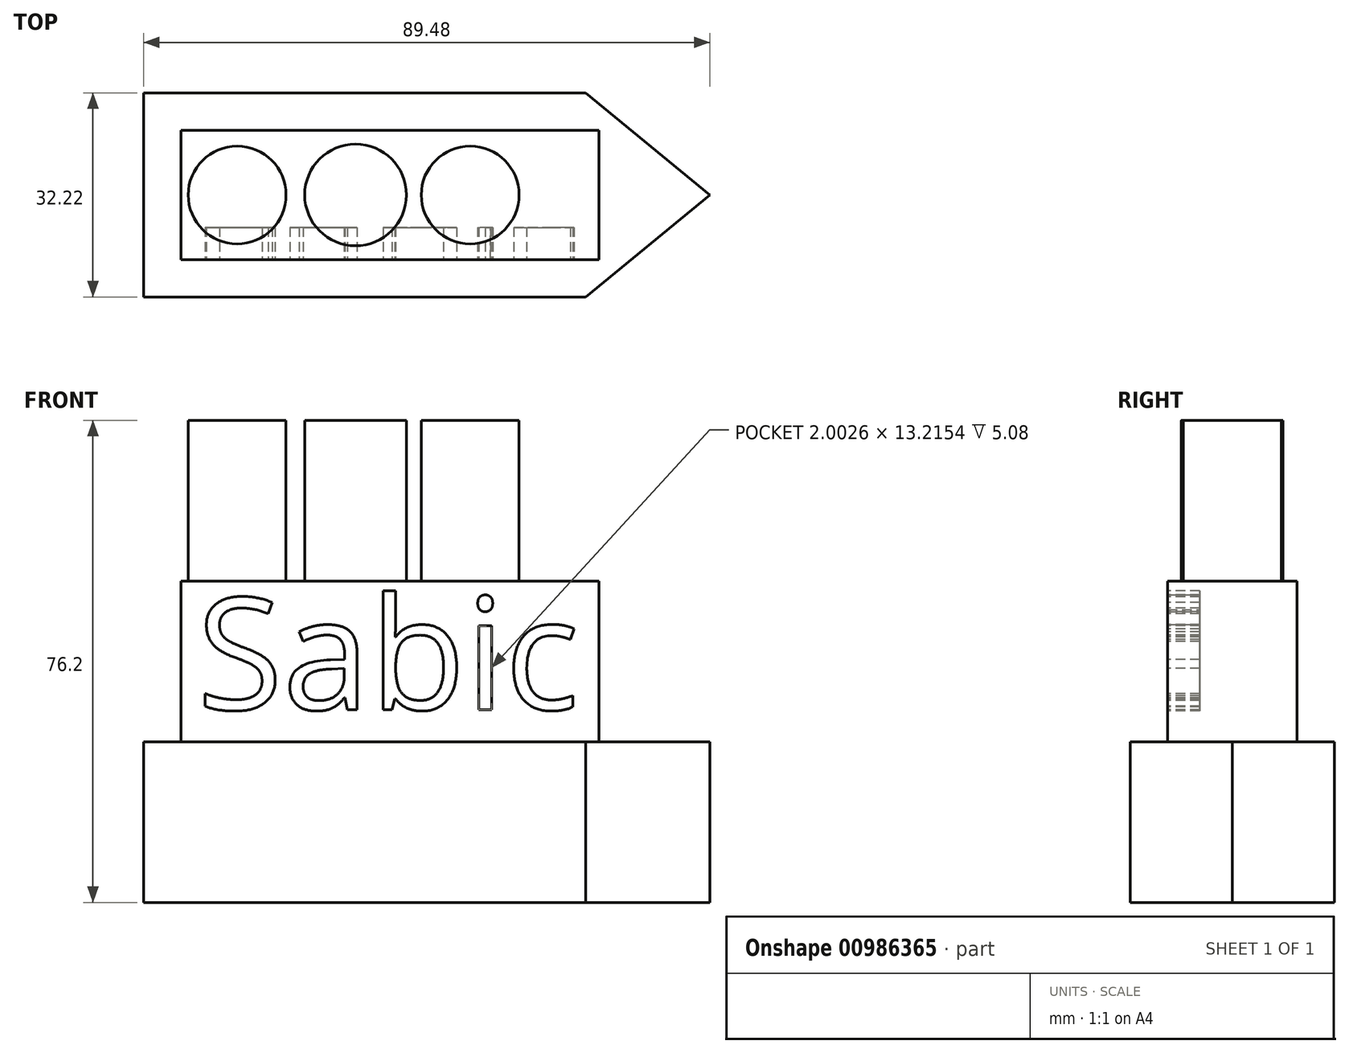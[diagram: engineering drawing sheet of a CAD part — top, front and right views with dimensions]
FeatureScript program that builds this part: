
annotation { "Feature Type Name" : "Feature", "Feature Type Description" : "" }
export const myFeature = defineFeature(function(context is Context, id is Id, definition is map)
    precondition{}
    {
        {
            var Q0;
            Q0=qCreatedBy(makeId("Top.planeOp"),FACE);
            var sketch = newSketch(context, id + "F0", { "sketchPlane" : qUnion([Q0])});
            skLineSegment(sketch, "E0", {"start": v(-58.68, 16.11) * mm, "end": v(11.17, 16.11) * mm});
            skLineSegment(sketch, "E1", {"start": v(11.17, 16.11) * mm, "end": v(30.8, 0) * mm});
            skLineSegment(sketch, "E2", {"start": v(30.8, 0) * mm, "end": v(11.17, -16.11) * mm});
            skLineSegment(sketch, "E3", {"start": v(11.17, -16.11) * mm, "end": v(-58.68, -16.11) * mm});
            skLineSegment(sketch, "E4", {"start": v(-58.68, -16.11) * mm, "end": v(-58.68, 16.11) * mm});
            skSolve(sketch);
        }
        {
            var Q0;
            Q0 = qSketchRegion(id + "F0", true);
            extrude(context, id + "F1", {"entities" : qUnion([Q0]), "depth" : 25.4 * mm, "offsetDistance" : 25.4 * mm});
        }
        {
            var Q0;
            Q0=qCreatedBy(makeId("Top.planeOp"),FACE);
            var sketch = newSketch(context, id + "F2", { "sketchPlane" : qUnion([Q0])});
            skLineSegment(sketch, "E5", {"start": v(-52.8, 10.22) * mm, "end": v(13.25, 10.22) * mm});
            skLineSegment(sketch, "E6", {"start": v(13.25, 10.22) * mm, "end": v(13.25, -10.22) * mm});
            skLineSegment(sketch, "E7", {"start": v(-52.8, -10.22) * mm, "end": v(-52.8, 10.22) * mm});
            skLineSegment(sketch, "E8", {"start": v(13.25, -10.22) * mm, "end": v(-52.8, -10.22) * mm});
            skSolve(sketch);
        }
        {
            var Q0;
            Q0 = qSketchRegion(id + "F2", true);
            extrude(context, id + "F3", {"entities" : qUnion([Q0]), "operationType" : NewBodyOperationType.ADD, "depth" : 50.8 * mm, "offsetDistance" : 25.4 * mm});
        }
        {
            var Q0;
            Q0=qCreatedBy(makeId("Top.planeOp"),FACE);
            var sketch = newSketch(context, id + "F4", { "sketchPlane" : qUnion([Q0])});
            skCircle(sketch, "E9", {"center": v(-43.9, 0) * mm, "radius": 7.73 * mm});
            skSolve(sketch);
        }
        {
            var Q0;
            Q0=qCreatedBy(makeId("Top.planeOp"),FACE);
            var sketch = newSketch(context, id + "F5", { "sketchPlane" : qUnion([Q0])});
            skCircle(sketch, "E10", {"center": v(-25.18, 0) * mm, "radius": 8.03 * mm});
            skSolve(sketch);
        }
        {
            var Q0;
            Q0 = qSketchRegion(id + "F4", true);
            extrude(context, id + "F6", {"entities" : qUnion([Q0]), "operationType" : NewBodyOperationType.ADD, "depth" : 76.2 * mm, "offsetDistance" : 25.4 * mm});
        }
        {
            var Q0;
            Q0 = qSketchRegion(id + "F5", true);
            extrude(context, id + "F7", {"entities" : qUnion([Q0]), "operationType" : NewBodyOperationType.ADD, "depth" : 76.2 * mm, "offsetDistance" : 25.4 * mm});
        }
        {
            var Q0;
            Q0=qCreatedBy(makeId("Top.planeOp"),FACE);
            var sketch = newSketch(context, id + "F8", { "sketchPlane" : qUnion([Q0])});
            skCircle(sketch, "E11", {"center": v(-7.07, 0) * mm, "radius": 7.73 * mm});
            skSolve(sketch);
        }
        {
            var Q0;
            Q0 = qSketchRegion(id + "F8", true);
            extrude(context, id + "F9", {"entities" : qUnion([Q0]), "operationType" : NewBodyOperationType.ADD, "depth" : 76.2 * mm, "offsetDistance" : 25.4 * mm});
        }
        {
            var Q0;
            Q0=makeQuery(id+"F3.opExtrude","SWEPT_FACE",FACE,{"disambiguationData":[OSD([sQuery(id+"F2.wireOp",EDGE,"E8")])]});
            var sketch = newSketch(context, id + "F10", { "sketchPlane" : qUnion([Q0])});
            skText(sketch, "E12", { "text": "Sabic", "fontName": "OpenSans-Regular.ttf"});
            const initialGuessF10  = {"E12": [-0.05025, 0.03048, 1, 0, 0.01778]};
            skSetInitialGuess(sketch, initialGuessF10);
            skSolve(sketch);
        }
        {
            var Q0;
            Q0 = qSketchRegion(id + "F10", true);
            extrude(context, id + "F11", {"entities" : qUnion([Q0]), "operationType" : NewBodyOperationType.REMOVE, "oppositeDirection" : true, "depth" : 5.08 * mm, "offsetDistance" : 25.4 * mm});
        }
    });
